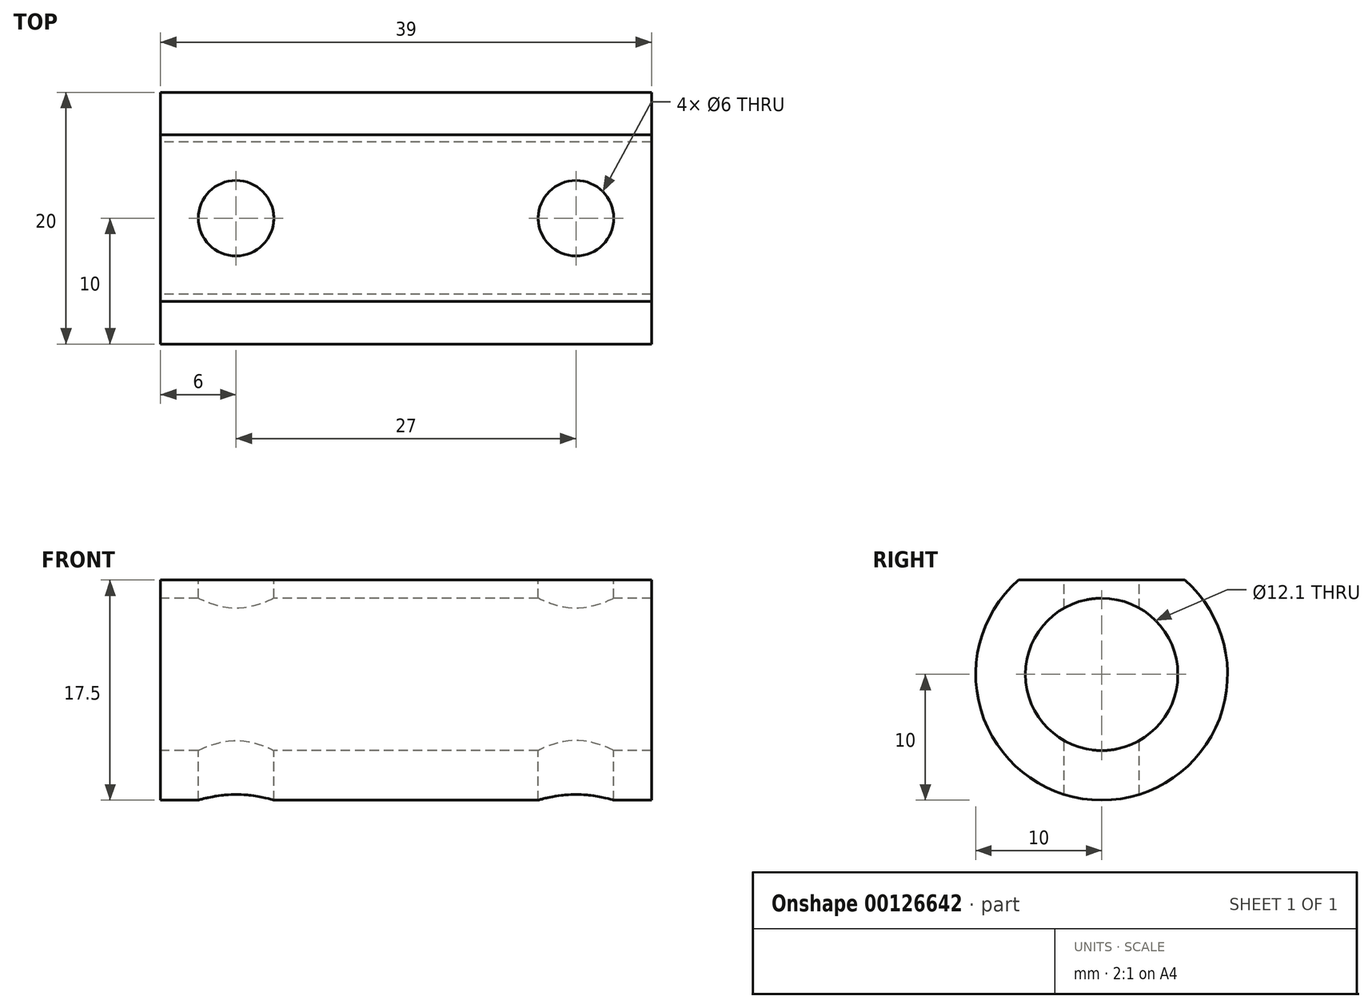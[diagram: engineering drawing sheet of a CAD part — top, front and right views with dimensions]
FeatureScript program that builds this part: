
annotation { "Feature Type Name" : "Feature", "Feature Type Description" : "" }
export const myFeature = defineFeature(function(context is Context, id is Id, definition is map)
    precondition{}
    {
        {
            var Q0;
            Q0=qCreatedBy(makeId("Right.planeOp"),FACE);
            var sketch = newSketch(context, id + "F0", { "sketchPlane" : qUnion([Q0])});
            skArc(sketch, "E0", {"start": v(-6.61, 7.5) * mm, "mid": v(0, -10) * mm, "end": v(6.61, 7.5) * mm});
            skCircle(sketch, "E1", {"center": v(0, 0) * mm, "radius": 6.05 * mm});
            skLineSegment(sketch, "E2", {"start": v(-6.61, 7.5) * mm, "end": v(6.61, 7.5) * mm});
            skSolve(sketch);
        }
        {
            var Q0;
            Q0=qSketchRegion(id+"F0",true);
            extrude(context, id + "F1", {"entities" : qUnion([Q0]), "depth" : 39 * mm});
        }
        {
            var Q0;
            Q0=makeQuery(id+"F1.opExtrude","SWEPT_FACE",FACE,{"disambiguationData":[OSD([sQuery(id+"F0.wireOp",EDGE,"E2")])]});
            var sketch = newSketch(context, id + "F2", { "sketchPlane" : qUnion([Q0])});
            skPoint(sketch, "E3", {"position": v(6, 0) * mm});
            skPoint(sketch, "E4", {"position": v(33, 0) * mm});
            skSolve(sketch);
        }
        {
            var Q0;
            Q0=sQuery(id+"F2.wireOp",VERTEX,"E3");
            var Q1;
            Q1=sQuery(id+"F2.wireOp",VERTEX,"E4");
            var Q2;
            Q2=makeQuery(id+"F1.opExtrude","SWEPT_BODY",BODY,{"disambiguationData":[OSD([sQuery(id+"F0.wireOp",EDGE,"E0"),sQuery(id+"F0.wireOp",EDGE,"E1"),sQuery(id+"F0.wireOp",EDGE,"E2")])]});
            hole(context, id + "F3", {"style" : HoleStyle.SIMPLE, "endStyle" : HoleEndStyle.THROUGH, "holeDiameter" : 6 * mm, "locations" : qUnion([Q0, Q1]), "scope" : qUnion([Q2]), "isTappedThrough" : true});
        }
    });
